# Revit family: VT.0606.0
name_source: partatom
category: Оборудование
units: mm (PartAtom-declared; Revit-internal decimal feet)

## family parameters
Всегда вертикально = Да
Заголовок OmniClass = Climate Control (HVAC)
На основе рабочей плоскости = Нет
Номер OmniClass = 23.75.00.00
Общий = Нет
При загрузке вырезать с полостями = Нет
Размер круглого соединителя = Использовать диаметр
Тип детали = Нормальный
Точка расчета площади = Нет

## types (2) — shared parameters
BIMобъект основная категория = Водопровод
EMCS Version = 3.0
IFC классификация = Клапан
Product Line = ТЕПЛОВАЯ ЭЛЕКТРОСТАНЦИЯ
Revit Version = 2018
SKU продукта = VARIMIX
URL бренда = https://valtec.ru
Uniclass 1.4 Описание = Климат-контроль установки и оборудование (HVAC)
Uniclass 2.0 Описание = Клапан
Uniformat II Description = HVAC
Вес нетто (кг) = 0
Группа модели = VT.0606.0
Группа товаров = VARIMIX
Изготовитель = IVAR
Инструкция по установке = https://valtec.ru
Мастерформат 2014 Описание = Отопление, вентиляция и кондиционирование воздуха (HVAC)
Описание = Сдвоенные ниппели
Описание NBS = Клапан
Описание OmniClass = HVAC Специальные продукты и оборудование
Описание статьи = Сдвоенные ниппели
Произведено в = Сделано в италии
Семейство продуктов = Тепловая электростанция
Системы отопления, охлаждения и охлаждения = Системы отопления, охлаждения и охлаждения
Страна изготовитель = Italy
Техническое описание = https://valtec.ru
Тип статьи = VT.0606.0
zero-valued in all types: Номинальная высота, Номинальная ширина

## per-type parameters (varying)
| type | BIMобъект категории | Finishing | URL | Код категории BIMобъекта | Код основной категории BIMobject | Материал | Материал основной | Описание Конфигурации | Практическое руководство по использованию семьи | Размер соединения |
| Yellow | Другое | BRASS - CW617N |  | Водопроводным-другой | Водопровод | Brass - CW617N | Brass | Сдвоенные ниппели | Вы должны выбрать один и только один тип отделочного материала для ротационного соска "мужчина-мужчина". Отметьте эту опцию в «Название типа - Никель»  или «Название типа - Желтый». | 1"1/4 |
| Nickel | Другие | Brass - Nickel | https://valtec.ru | водопроводным-другой | водопровод | Никелированная латунь - CW617N | Латунь | Мужской мужской роторный сосок. | - Вы должны выбрать один и только один тип отделочного материала для ротационного соска "мужчина-мужчина". Отметьте эту опцию в «Название типа - Никель» или «Название типа - Желтый». | G 1"1/4 M |
